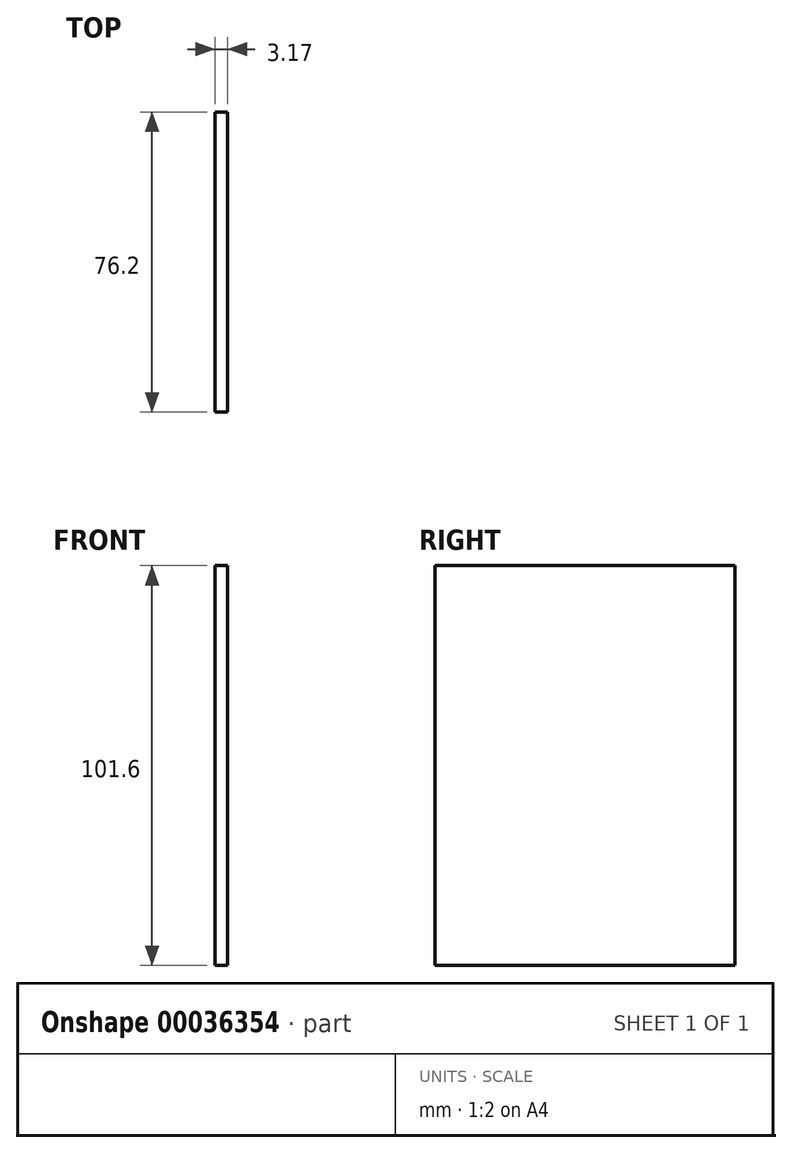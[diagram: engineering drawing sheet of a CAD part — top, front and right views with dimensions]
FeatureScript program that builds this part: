
annotation { "Feature Type Name" : "Feature", "Feature Type Description" : "" }
export const myFeature = defineFeature(function(context is Context, id is Id, definition is map)
    precondition{}
    {
        {
            var Q0;
            Q0=qCreatedBy(makeId("Right.planeOp"),FACE);
            var sketch = newSketch(context, id + "F0", { "sketchPlane" : qUnion([Q0])});
            skLineSegment(sketch, "E0.rect.bottom", {"start": v(-38.1, 50.8) * mm, "end": v(38.1, 50.8) * mm});
            skLineSegment(sketch, "E0.rect.top", {"start": v(-38.1, -50.8) * mm, "end": v(38.1, -50.8) * mm});
            skLineSegment(sketch, "E0.rect.left", {"start": v(-38.1, 50.8) * mm, "end": v(-38.1, -50.8) * mm});
            skLineSegment(sketch, "E0.rect.right", {"start": v(38.1, 50.8) * mm, "end": v(38.1, -50.8) * mm});
            skPoint(sketch, "E0.rect.middle", {"position": v(0, 0) * mm});
            skSolve(sketch);
        }
        {
            var Q0;
            Q0=makeQuery(id+"F0.imprint","IMPRINT",FACE,{"disambiguationData":[TD([[makeQuery(id+"F0.imprint","IMPRINT",EDGE,{"derivedFrom":sQuery(id+"F0.wireOp",EDGE,"E0.rect.bottom")}),-1.0]])]});
            extrude(context, id + "F1", {"entities" : qUnion([Q0]), "depth" : 3.17 * mm});
        }
    });
